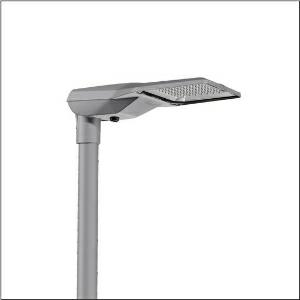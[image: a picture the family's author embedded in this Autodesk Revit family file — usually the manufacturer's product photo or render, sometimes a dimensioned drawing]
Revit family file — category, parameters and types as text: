
# Revit family: streetlight_sl_21_midi___p0_8ab_5xe3r33r08lb_93be
name_source: partatom
category: Lighting Fixtures
units: mm (PartAtom-declared; Revit-internal decimal feet)

## family parameters
Cut with Voids When Loaded = No
Host = Face
Light Source = No
Part Type = Normal
Room Calculation Point = No
Round Connector Dimension = Use Diameter
Shared = No

## types (1)
- --- (1 x LED, 12450 lm, 99.6 W, 3000K)
    Apparent Load = 100 VA
    CIE Flux Codes = 36 71 98 100 100
    Color Rendering = 70
    Color Temperature = 3000K
    Default Elevation = 1800 mm
    Description = Streetlight SL 21 midi, mast luminaire, primary light control with lens, of PMMA, primary optical cover: cover, of toughened safety glass, transparent, light distribution: P0.8aB, light emission: direct distribution, primary light characteristic: asymmetric, installation type: post-top, side-entry, LED, High Power LED, rated luminous flux: 12.450lm, luminous efficacy: 125lm/W, light colour: 730, colour temperature: 3000K, control gear: D4i, control: pre-setting: logarithmic dimming characteristic, flexible luminous flux parameterisation, time-dependent luminous flux control, constant luminous flux control, overheat protection, mains connection: 230..240V, AC, 50/60Hz, start of lifetime: 100W, end of service life: 102W, reduction: 46W, luminaire housing, of diecast aluminium, powder-coated, Siteco® metallic grey (DB 702S), corrosivity category C5 mid according to DIN EN ISO 12944, multi-level sealing system, sealing non-destructively replaceable, inclination adjustable: 0°, 5°, 10°, 15°, please order mast flange separately, length: 644mm, width: 335mm, height: 110mm, mast flange for spigot size: 42mm (side-entry): 5XC10008XM4, 60/48mm (side-entry/post-top): 5XC10108XM2, 76/60mm (side-entry/post-top): 5XC10108XM1, mounting height: 4..8m, Smart Interface below, protection rating (complete): IP66, insulation class (complete): insulation class II (safety insulation), certification: CE, ENEC, ENEC+, VDE, impact resistance: IK10, permissible operating ambient temperature for outdoor applications: -40..+50°C, standard-compliant lighting for roads and squares, packaging unit: 1 piece

Light Distribution: P0.8aB
    Height = 111 mm
    Lamp = 1 x LED
    Lamp Light Flux = 12450 lm
    Lamp Power = 99.6 W
    Lamp count = 1
    Length = 644 mm
    Luminous efficacy = 125 lm/W
    Manufacturer = Siteco
    ModVariant = No
    Model = 5XE3R33R08LB
    Number of Poles = 1
    OnlyDefault = Yes
    Power Factor = 1
    Product Name = Streetlight SL 21 midi | P0.8aB
    Product group = mast luminaire | pylon top
    ProductGroupID = 6100
    Protection Class = Protection class II
    Protection Degree = IP 66
    RLX_Detail_Level = 1
    RLX_Emergency_Light_Flux = 0 lm
    RLX_Emergency_Type = 0
    RLX_Emergency_Type_DB = No
    RlxData = <blob elided: 26505 chars, md5=85ed3c0f>
    Socket = socket
    Standby Power = 0 W
    System Light Flux = 12450 lm
    System Power = 100 W
    Type Comments = factory setting: luminous flux: 100 % | dim-lin: 254 | 1020 mA
    Type Image = l_1004300.jpg
    URL = http://relux.com
    VarID = @adj_033585
    Voltage = 0 V
    Weight = 0.00 kg
    Width = 336 mm

## geometry (parser evidence)
native form markers: Blend x4, Sweep x10
no freeform markers — native parametric forms only
